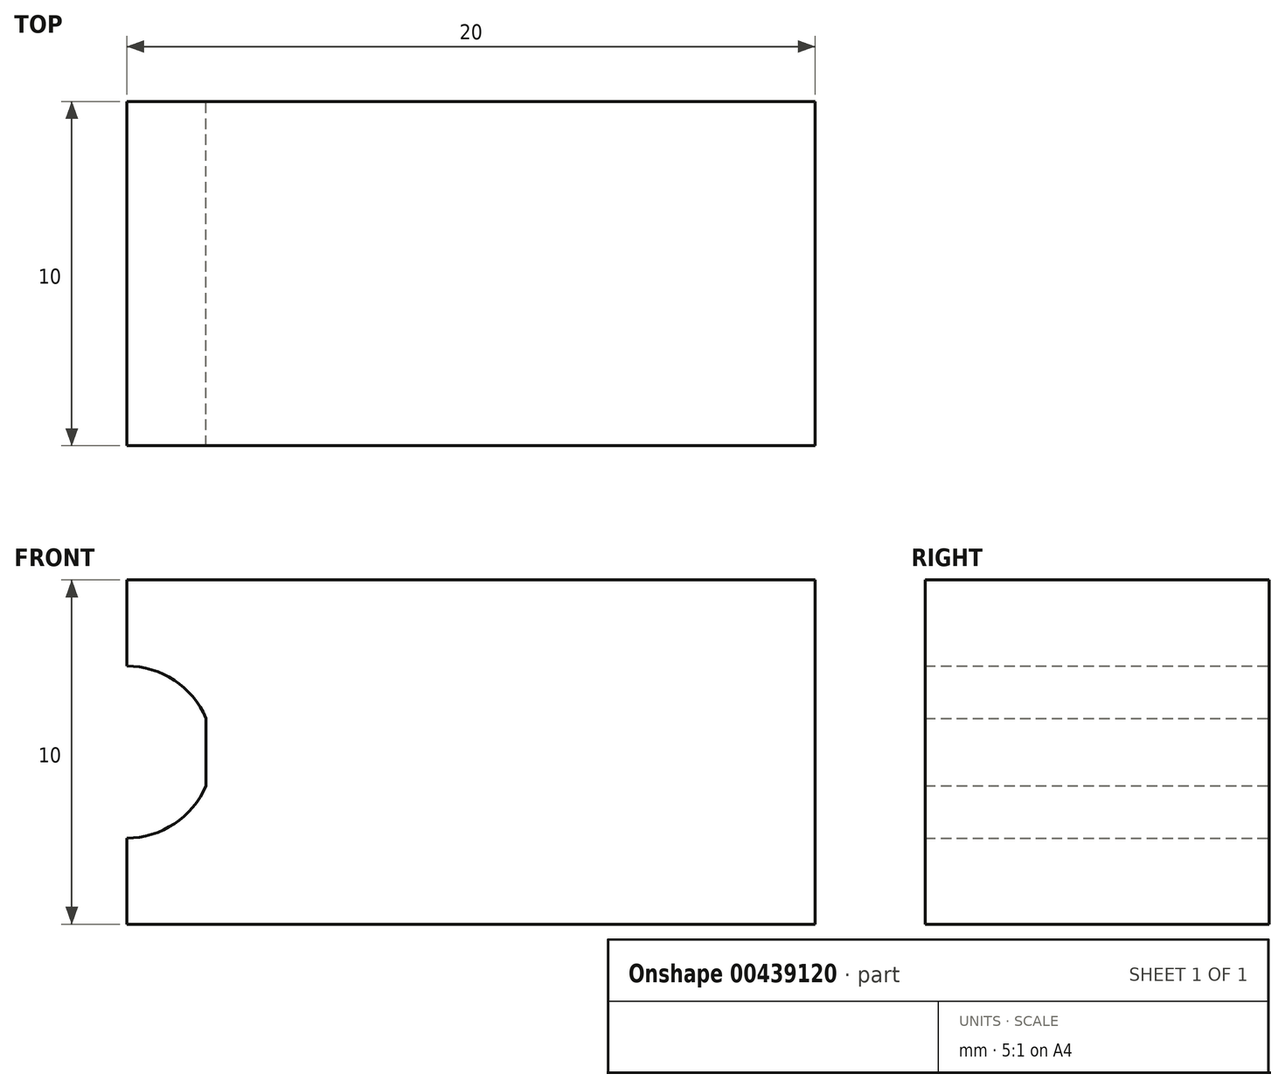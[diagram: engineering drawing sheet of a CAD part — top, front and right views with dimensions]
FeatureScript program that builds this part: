
annotation { "Feature Type Name" : "Feature", "Feature Type Description" : "" }
export const myFeature = defineFeature(function(context is Context, id is Id, definition is map)
    precondition{}
    {
        {
            var Q0;
            Q0=qCreatedBy(makeId("Front.planeOp"),FACE);
            var sketch = newSketch(context, id + "F0", { "sketchPlane" : qUnion([Q0])});
            skLineSegment(sketch, "E0", {"start": v(0, 0) * mm, "end": v(20, 0) * mm});
            skLineSegment(sketch, "E1", {"start": v(20, 0) * mm, "end": v(20, 10) * mm});
            skLineSegment(sketch, "E2", {"start": v(20, 10) * mm, "end": v(0, 10) * mm});
            skLineSegment(sketch, "E3", {"start": v(0, 10) * mm, "end": v(0, 0) * mm, "construction": true});
            skArc(sketch, "E4", {"start": v(0, 7.5) * mm, "mid": v(2.5, 5) * mm, "end": v(0, 2.5) * mm});
            skLineSegment(sketch, "E5", {"start": v(0, 5) * mm, "end": v(2.3, 5) * mm, "construction": true});
            skLineSegment(sketch, "E6", {"start": v(2.3, 4.02) * mm, "end": v(2.3, 5.98) * mm});
            skLineSegment(sketch, "E7", {"start": v(0, 7.5) * mm, "end": v(0, 10) * mm});
            skLineSegment(sketch, "E8", {"start": v(0, 2.5) * mm, "end": v(0, 0) * mm});
            skSolve(sketch);
        }
        {
            var Q0;
            {var subQ0=sQuery(id+"F0.wireOp",EDGE,"E6");Q0=makeQuery(id+"F0.imprint","IMPRINT",FACE,{"disambiguationData":[TD([[makeQuery(id+"F0.imprint","IMPRINT",EDGE,{"derivedFrom":subQ0}),-1.0]])]});}
            var Q1;
            Q1=makeQuery(id+"F0.imprint","IMPRINT",FACE,{"disambiguationData":[TD([[makeQuery(id+"F0.imprint","IMPRINT",EDGE,{"derivedFrom":sQuery(id+"F0.wireOp",EDGE,"E0")}),1.0]])]});
            extrude(context, id + "F1", {"entities" : qUnion([Q0, Q1]), "depth" : 10 * mm});
        }
    });
